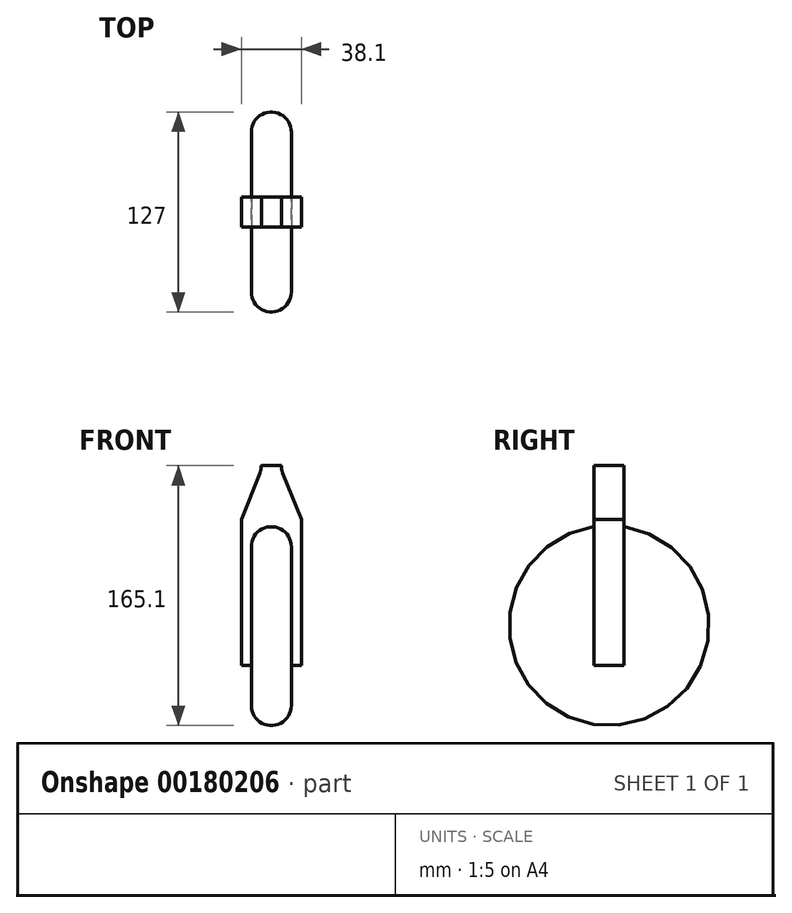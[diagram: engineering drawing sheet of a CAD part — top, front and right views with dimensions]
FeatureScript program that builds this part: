
annotation { "Feature Type Name" : "Feature", "Feature Type Description" : "" }
export const myFeature = defineFeature(function(context is Context, id is Id, definition is map)
    precondition{}
    {
        {
            var Q0;
            Q0=qCreatedBy(makeId("Right.planeOp"),FACE);
            var sketch = newSketch(context, id + "F0", { "sketchPlane" : qUnion([Q0])});
            skCircle(sketch, "E0", {"center": v(0, 0) * mm, "radius": 6.35 * mm});
            skCircle(sketch, "E1", {"center": v(0, 0) * mm, "radius": 63.5 * mm});
            skSolve(sketch);
        }
        {
            var Q0;
            Q0 = qSketchRegion(id + "F0", true);
            extrude(context, id + "F1", {"entities" : qUnion([Q0]), "endBound" : BoundingType.SYMMETRIC, "depth" : 25.4 * mm});
        }
        {
            var Q0;
            Q0=makeQuery(id+"F1.opExtrude","CAP_EDGE",EDGE,{"disambiguationData":[OSD([sQuery(id+"F0.wireOp",EDGE,"E1")])],"isStart":true});
            var Q1;
            Q1=makeQuery(id+"F1.opExtrude","CAP_EDGE",EDGE,{"disambiguationData":[OSD([sQuery(id+"F0.wireOp",EDGE,"E1")])],"isStart":false});
            fillet(context, id + "F2", {"entities" : qUnion([Q0, Q1]), "radius" : 12.7 * mm, "tangentPropagation" : true, "allowEdgeOverflow" : false});
        }
        {
            var Q0;
            Q0=qCreatedBy(makeId("Front.planeOp"),FACE);
            var sketch = newSketch(context, id + "F3", { "sketchPlane" : qUnion([Q0])});
            skLineSegment(sketch, "E2.bottom", {"start": v(6.35, 101.6) * mm, "end": v(-6.35, 101.6) * mm});
            skLineSegment(sketch, "E2.left", {"start": v(19.05, 67.2) * mm, "end": v(19.05, -25.31) * mm});
            skLineSegment(sketch, "E2.right", {"start": v(-19.05, 67.2) * mm, "end": v(-19.05, -25.31) * mm});
            skPoint(sketch, "E2.middle", {"position": v(0, 0) * mm});
            skLineSegment(sketch, "E3", {"start": v(-19.05, -25.31) * mm, "end": v(19.05, -25.31) * mm});
            skPoint(sketch, "E2.top.end.orphan", {"position": v(-19.05, -101.6) * mm});
            skPoint(sketch, "E2.top.start.orphan", {"position": v(19.05, -101.6) * mm});
            skArc(sketch, "E4", {"start": v(-7.25, 96.91) * mm, "mid": v(-6.58, 99.21) * mm, "end": v(-6.35, 101.6) * mm});
            skArc(sketch, "E5", {"start": v(6.35, 101.6) * mm, "mid": v(6.58, 99.21) * mm, "end": v(7.25, 96.91) * mm});
            skLineSegment(sketch, "E6", {"start": v(-19.05, 67.2) * mm, "end": v(-7.25, 96.91) * mm});
            skLineSegment(sketch, "E7", {"start": v(19.05, 67.2) * mm, "end": v(7.25, 96.91) * mm});
            skSolve(sketch);
        }
        {
            var Q0;
            Q0 = qSketchRegion(id + "F3", true);
            extrude(context, id + "F4", {"entities" : qUnion([Q0]), "operationType" : NewBodyOperationType.ADD, "endBound" : BoundingType.SYMMETRIC, "depth" : 19.05 * mm});
        }
    });
